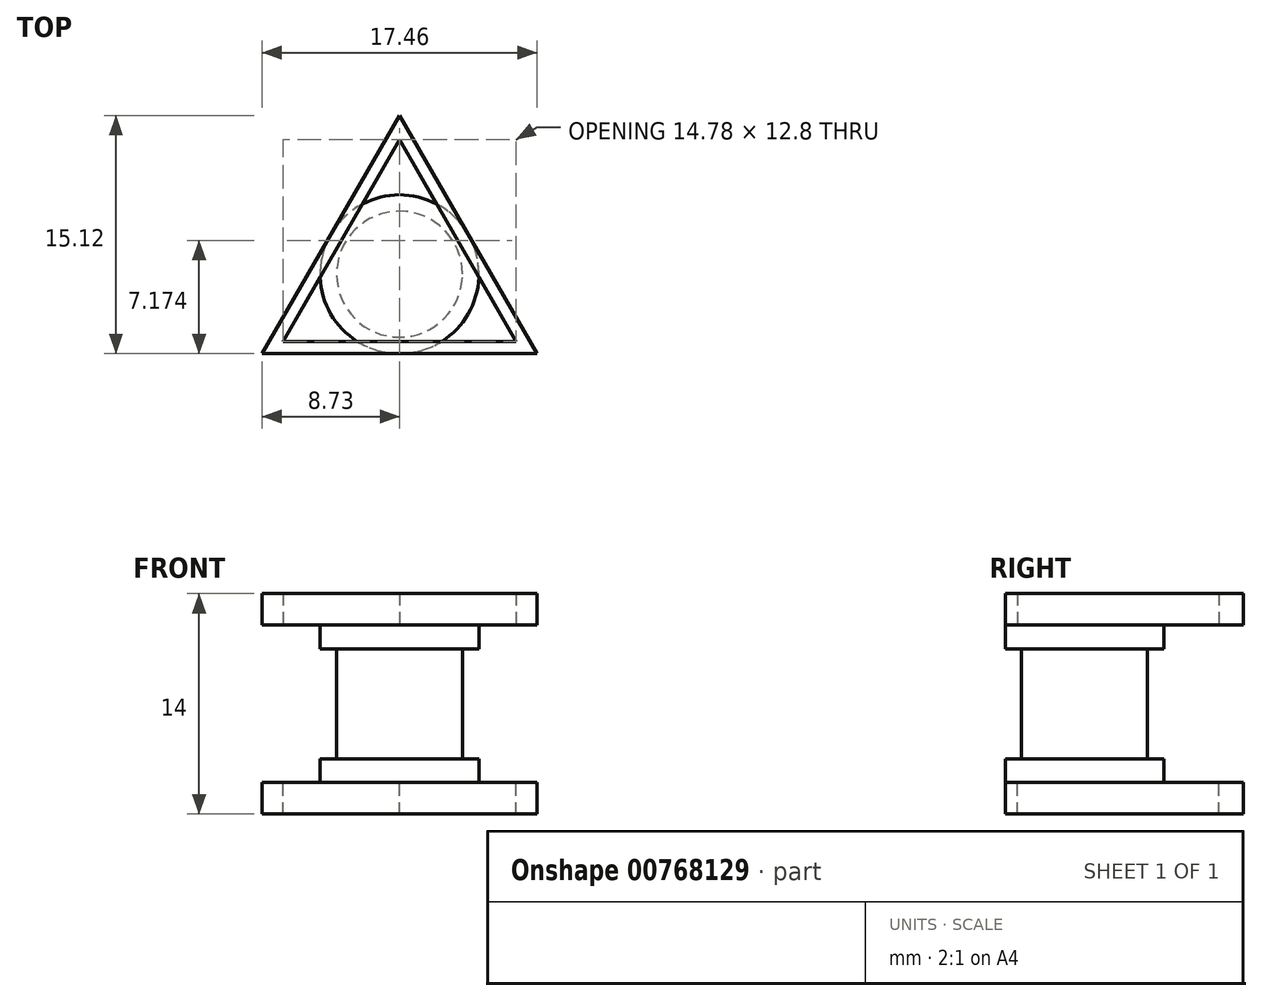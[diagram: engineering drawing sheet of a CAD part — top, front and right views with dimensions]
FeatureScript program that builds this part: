
annotation { "Feature Type Name" : "Feature", "Feature Type Description" : "" }
export const myFeature = defineFeature(function(context is Context, id is Id, definition is map)
    precondition{}
    {
        {
            var Q0;
            Q0=qCreatedBy(makeId("Top.planeOp"),FACE);
            var sketch = newSketch(context, id + "F0", { "sketchPlane" : qUnion([Q0])});
            skCircle(sketch, "E0", {"center": v(0, 0) * mm, "radius": 4 * mm});
            skCircle(sketch, "E1", {"center": v(0, 0) * mm, "radius": 5 * mm});
            skSolve(sketch);
        }
        {
            var Q0;
            Q0=makeQuery(id+"F0.imprint","IMPRINT",FACE,{"disambiguationData":[TD([[makeQuery(id+"F0.imprint","IMPRINT",EDGE,{"derivedFrom":sQuery(id+"F0.wireOp",EDGE,"E0")}),1.0]])]});
            extrude(context, id + "F1", {"entities" : qUnion([Q0]), "depth" : 3.5 * mm, "offsetDistance" : 25 * mm});
        }
        {
            var Q0;
            Q0=makeQuery(id+"F1.opExtrude","CAP_FACE",FACE,{"disambiguationData":[OSD([sQuery(id+"F0.wireOp",EDGE,"E0")])],"isStart":false});
            var sketch = newSketch(context, id + "F2", { "sketchPlane" : qUnion([Q0])});
            skCircle(sketch, "E2", {"center": v(0, 0) * mm, "radius": 5.04 * mm});
            skSolve(sketch);
        }
        {
            var Q0;
            Q0=makeQuery(id+"F2.imprint","IMPRINT",FACE,{"disambiguationData":[TD([[makeQuery(id+"F2.imprint","IMPRINT",EDGE,{"derivedFrom":sQuery(id+"F2.wireOp",EDGE,"E2")}),1.0]])]});
            var Q1;
            Q1=makeQuery(id+"F2.imprint","IMPRINT",FACE,{"disambiguationData":[TD([[makeQuery(id+"F2.imprint","IMPRINT",EDGE,{"derivedFrom":makeQuery(id+"F1.opExtrude","CAP_EDGE",EDGE,{"disambiguationData":[OSD([sQuery(id+"F0.wireOp",EDGE,"E0")])],"isStart":false})}),1.0]])]});
            var Q2;
            Q2=sQuery(id+"F2.wireOp",EDGE,"E2");
            extrude(context, id + "F3", {"entities" : qUnion([Q0, Q1]), "operationType" : NewBodyOperationType.ADD, "surfaceEntities" : qUnion([Q2]), "depth" : 1.5 * mm, "offsetDistance" : 25 * mm});
        }
        {
            var Q0;
            Q0=makeQuery(id+"F3.opExtrude","CAP_FACE",FACE,{"disambiguationData":[OSD([sQuery(id+"F2.wireOp",EDGE,"E2")])],"isStart":false});
            var sketch = newSketch(context, id + "F4", { "sketchPlane" : qUnion([Q0])});
            skCircle(sketch, "E3.cCircle", {"center": v(0, 0) * mm, "radius": 5.04 * mm, "construction": true});
            skLineSegment(sketch, "E3.0", {"start": v(8.73, -5.04) * mm, "end": v(-8.73, -5.04) * mm});
            skLineSegment(sketch, "E3.1", {"start": v(-8.73, -5.04) * mm, "end": v(0, 10.08) * mm});
            skLineSegment(sketch, "E3.2", {"start": v(0, 10.08) * mm, "end": v(8.73, -5.04) * mm});
            skPoint(sketch, "E3.0.midPoint", {"position": v(0, -5.04) * mm});
            skCircle(sketch, "E4.cCircle", {"center": v(0, 0) * mm, "radius": 4.27 * mm, "construction": true});
            skLineSegment(sketch, "E4.0", {"start": v(7.4, -4.27) * mm, "end": v(-7.4, -4.27) * mm});
            skLineSegment(sketch, "E4.1", {"start": v(-7.4, -4.27) * mm, "end": v(0, 8.54) * mm});
            skLineSegment(sketch, "E4.2", {"start": v(0, 8.54) * mm, "end": v(7.4, -4.27) * mm});
            skPoint(sketch, "E4.0.midPoint", {"position": v(0, -4.27) * mm});
            skSolve(sketch);
        }
        {
            var Q0;
            {var subQ0=sQuery(id+"F4.wireOp",EDGE,"E4.1");var subQ1=makeQuery(id+"F3.opExtrude","CAP_EDGE",EDGE,{"disambiguationData":[OSD([sQuery(id+"F2.wireOp",EDGE,"E2")])],"isStart":false});var subQ2=makeQuery(id+"F4.imprint","INTERSECT",VERTEX,{"disambiguationData":[OD(0.0)],"derivedFrom":[subQ1,subQ0]});Q0=makeQuery(id+"F4.imprint","IMPRINT",FACE,{"disambiguationData":[TD([[makeQuery(id+"F4.imprint","IMPRINT",EDGE,{"disambiguationData":[TD([[subQ2,-1.0]])],"derivedFrom":subQ0}),1.0]])]});}
            var Q1;
            {var subQ0=sQuery(id+"F4.wireOp",EDGE,"E4.0");var subQ1=makeQuery(id+"F3.opExtrude","CAP_EDGE",EDGE,{"disambiguationData":[OSD([sQuery(id+"F2.wireOp",EDGE,"E2")])],"isStart":false});var subQ2=makeQuery(id+"F4.imprint","INTERSECT",VERTEX,{"disambiguationData":[OD(0.0)],"derivedFrom":[subQ1,subQ0]});Q1=makeQuery(id+"F4.imprint","IMPRINT",FACE,{"disambiguationData":[TD([[makeQuery(id+"F4.imprint","IMPRINT",EDGE,{"disambiguationData":[TD([[subQ2,-1.0]])],"derivedFrom":subQ0}),1.0]])]});}
            var Q2;
            {var subQ0=sQuery(id+"F4.wireOp",EDGE,"E4.2");var subQ1=makeQuery(id+"F3.opExtrude","CAP_EDGE",EDGE,{"disambiguationData":[OSD([sQuery(id+"F2.wireOp",EDGE,"E2")])],"isStart":false});var subQ2=makeQuery(id+"F4.imprint","INTERSECT",VERTEX,{"disambiguationData":[OD(0.0)],"derivedFrom":[subQ1,subQ0]});Q2=makeQuery(id+"F4.imprint","IMPRINT",FACE,{"disambiguationData":[TD([[makeQuery(id+"F4.imprint","IMPRINT",EDGE,{"disambiguationData":[TD([[subQ2,-1.0]])],"derivedFrom":subQ0}),1.0]])]});}
            var Q3;
            {var subQ6=sQuery(id+"F4.wireOp",EDGE,"E3.2");var subQ7=sQuery(id+"F4.wireOp",EDGE,"E3.1");var subQ8=makeQuery(id+"F4.imprint","INTERSECT",VERTEX,{"derivedFrom":[subQ7,subQ6]});Q3=makeQuery(id+"F4.imprint","IMPRINT",FACE,{"disambiguationData":[TD([[makeQuery(id+"F4.imprint","IMPRINT",EDGE,{"disambiguationData":[TD([[subQ8,1.0]])],"derivedFrom":subQ7}),-1.0]])]});}
            var Q4;
            {var subQ6=sQuery(id+"F4.wireOp",EDGE,"E3.1");var subQ7=sQuery(id+"F4.wireOp",EDGE,"E3.0");var subQ8=makeQuery(id+"F4.imprint","INTERSECT",VERTEX,{"derivedFrom":[subQ7,subQ6]});Q4=makeQuery(id+"F4.imprint","IMPRINT",FACE,{"disambiguationData":[TD([[makeQuery(id+"F4.imprint","IMPRINT",EDGE,{"disambiguationData":[TD([[subQ8,1.0]])],"derivedFrom":subQ7}),-1.0]])]});}
            var Q5;
            {var subQ6=sQuery(id+"F4.wireOp",EDGE,"E3.2");var subQ7=sQuery(id+"F4.wireOp",EDGE,"E3.0");var subQ8=makeQuery(id+"F4.imprint","INTERSECT",VERTEX,{"derivedFrom":[subQ7,subQ6]});Q5=makeQuery(id+"F4.imprint","IMPRINT",FACE,{"disambiguationData":[TD([[makeQuery(id+"F4.imprint","IMPRINT",EDGE,{"disambiguationData":[TD([[subQ8,-1.0]])],"derivedFrom":subQ7}),-1.0]])]});}
            extrude(context, id + "F5", {"entities" : qUnion([Q0, Q1, Q2, Q3, Q4, Q5]), "operationType" : NewBodyOperationType.ADD, "depth" : 2 * mm, "offsetDistance" : 25 * mm});
        }
        {
            var Q0;
            Q0=makeQuery(id+"F1.opExtrude","SWEPT_BODY",BODY,{"disambiguationData":[OSD([sQuery(id+"F0.wireOp",EDGE,"E0")])]});
            var Q1;
            Q1=qCreatedBy(makeId("Top.planeOp"),FACE);
            mirror(context, id + "F6", {"operationType" : NewBodyOperationType.ADD, "entities" : qUnion([Q0]), "mirrorPlane" : qUnion([Q1])});
        }
    });
